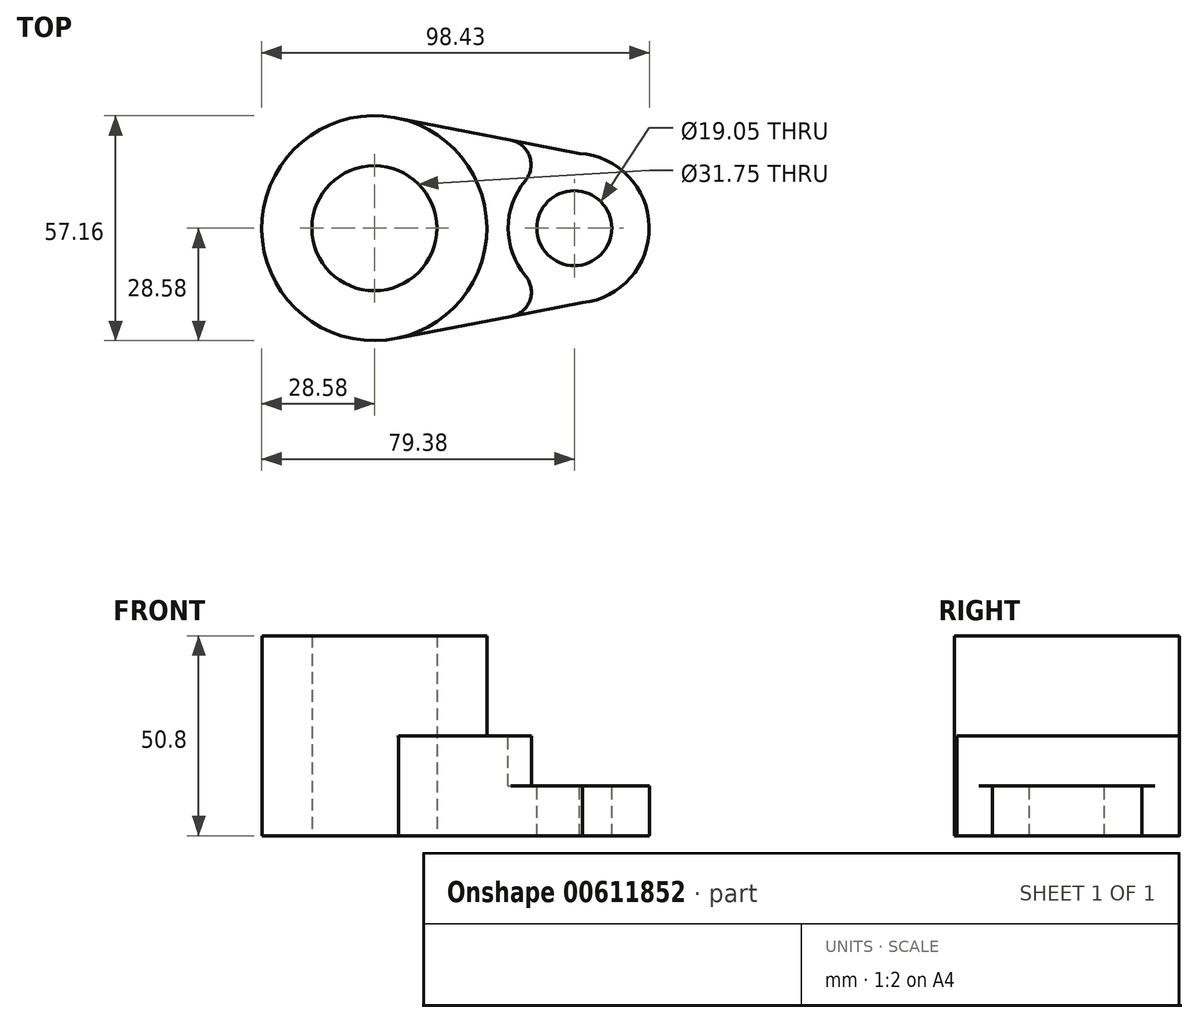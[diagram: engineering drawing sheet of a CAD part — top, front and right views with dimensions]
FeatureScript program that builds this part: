
annotation { "Feature Type Name" : "Feature", "Feature Type Description" : "" }
export const myFeature = defineFeature(function(context is Context, id is Id, definition is map)
    precondition{}
    {
        {
            var Q0;
            Q0=qCreatedBy(makeId("Top.planeOp"),FACE);
            var sketch = newSketch(context, id + "F0", { "sketchPlane" : qUnion([Q0])});
            skCircle(sketch, "E0", {"center": v(0, 0) * mm, "radius": 15.88 * mm});
            skCircle(sketch, "E1", {"center": v(0, 0) * mm, "radius": 28.58 * mm});
            skLineSegment(sketch, "E2", {"start": v(0, 0) * mm, "end": v(50.8, 0) * mm});
            skCircle(sketch, "E3", {"center": v(50.8, 0) * mm, "radius": 9.53 * mm});
            skCircle(sketch, "E4", {"center": v(50.8, 0) * mm, "radius": 19.05 * mm});
            skLineSegment(sketch, "E5", {"start": v(5.16, 28.1) * mm, "end": v(52.1, 19) * mm});
            skLineSegment(sketch, "E6", {"start": v(6.11, -27.91) * mm, "end": v(52.86, -18.94) * mm});
            skSolve(sketch);
        }
        {
            var Q0;
            Q0=makeQuery(id+"F0.imprint","IMPRINT",FACE,{"disambiguationData":[TD([[makeQuery(id+"F0.imprint","IMPRINT",EDGE,{"derivedFrom":sQuery(id+"F0.wireOp",EDGE,"E0")}),-1.0]])]});
            extrude(context, id + "F1", {"entities" : qUnion([Q0]), "depth" : 25.4 * mm, "offsetDistance" : 25.4 * mm});
        }
        {
            var Q0;
            Q0 = qSketchRegion(id + "F0", true);
            extrude(context, id + "F2", {"entities" : qUnion([Q0]), "operationType" : NewBodyOperationType.ADD, "oppositeDirection" : true, "depth" : 25.4 * mm, "offsetDistance" : 25.4 * mm});
        }
        {
            var Q0;
            Q0=makeQuery(id+"F2.opExtrude","CAP_FACE",FACE,{"disambiguationData":[OSD([sQuery(id+"F0.wireOp",EDGE,"E0"),sQuery(id+"F0.wireOp",EDGE,"E1"),sQuery(id+"F0.wireOp",EDGE,"E3"),sQuery(id+"F0.wireOp",EDGE,"E4"),sQuery(id+"F0.wireOp",EDGE,"E5"),sQuery(id+"F0.wireOp",EDGE,"E6")])],"isStart":true});
            var sketch = newSketch(context, id + "F3", { "sketchPlane" : qUnion([Q0])});
            skArc(sketch, "E7", {"start": v(52.1, 19) * mm, "mid": v(34.03, -0.34) * mm, "end": v(52.86, -18.94) * mm});
            skSolve(sketch);
        }
        {
            var Q0;
            Q0=makeQuery(id+"F3.imprint","IMPRINT",FACE,{"disambiguationData":[TD([[makeQuery(id+"F3.imprint","IMPRINT",EDGE,{"derivedFrom":sQuery(id+"F3.wireOp",EDGE,"E7")}),1.0]])]});
            extrude(context, id + "F4", {"entities" : qUnion([Q0]), "operationType" : NewBodyOperationType.REMOVE, "oppositeDirection" : true, "depth" : 12.7 * mm, "offsetDistance" : 25.4 * mm});
        }
        {
            var Q0;
            {var subQ0=sQuery(id+"F0.wireOp",EDGE,"E6");var subQ1=sQuery(id+"F0.wireOp",EDGE,"E4");Q0=makeQuery(id+"F4.boolean.opBoolean","MERGE",EDGE,{"derivedFrom":[makeQuery(id+"F2.opExtrude","SWEPT_EDGE",EDGE,{"disambiguationData":[OSD([subQ1,subQ0])]}),makeQuery(id+"F4.opExtrude","SWEPT_EDGE",EDGE,{"disambiguationData":[OSD([subQ1,subQ0,sQuery(id+"F3.wireOp",EDGE,"E7")])]})]});}
            var Q1;
            {var subQ0=sQuery(id+"F0.wireOp",EDGE,"E5");var subQ1=sQuery(id+"F0.wireOp",EDGE,"E4");Q1=makeQuery(id+"F4.boolean.opBoolean","MERGE",EDGE,{"derivedFrom":[makeQuery(id+"F2.opExtrude","SWEPT_EDGE",EDGE,{"disambiguationData":[OSD([subQ1,subQ0])]}),makeQuery(id+"F4.opExtrude","SWEPT_EDGE",EDGE,{"disambiguationData":[OSD([subQ1,subQ0,sQuery(id+"F3.wireOp",EDGE,"E7")])]})]});}
            fillet(context, id + "F5", {"entities" : qUnion([Q0, Q1]), "radius" : 6.35 * mm, "tangentPropagation" : true, "allowEdgeOverflow" : false});
        }
    });
